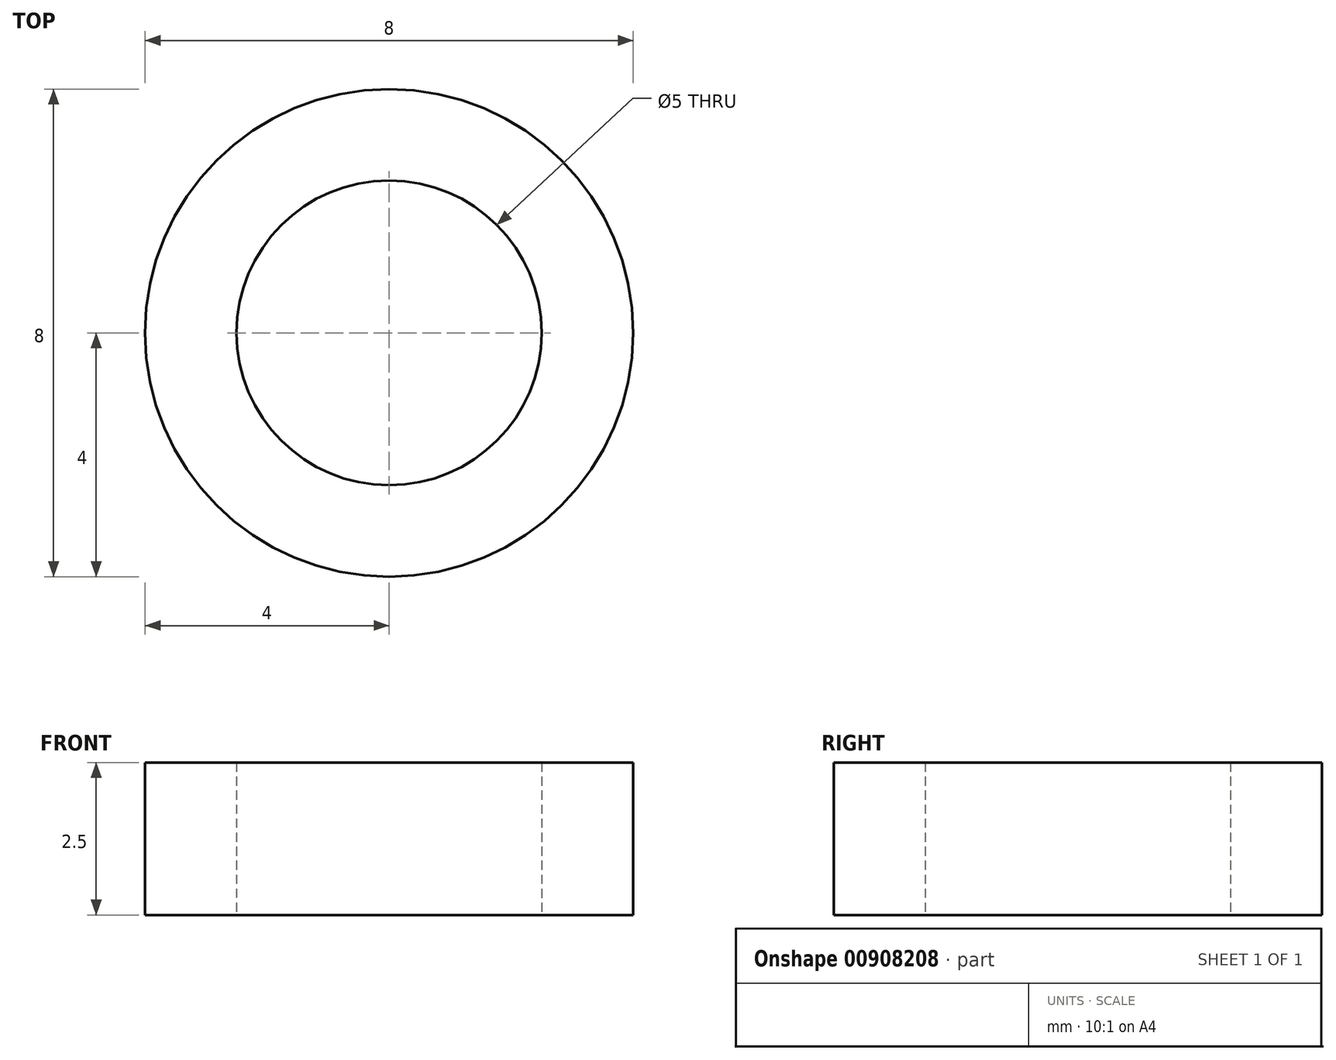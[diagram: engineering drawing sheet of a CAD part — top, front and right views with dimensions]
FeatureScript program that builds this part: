
annotation { "Feature Type Name" : "Feature", "Feature Type Description" : "" }
export const myFeature = defineFeature(function(context is Context, id is Id, definition is map)
    precondition{}
    {
        {
            var Q0;
            Q0=qCreatedBy(makeId("Top.planeOp"),FACE);
            var sketch = newSketch(context, id + "F0", { "sketchPlane" : qUnion([Q0])});
            skCircle(sketch, "E0", {"center": v(0, 0) * mm, "radius": 2.5 * mm});
            skCircle(sketch, "E1", {"center": v(0, 0) * mm, "radius": 4 * mm});
            skSolve(sketch);
        }
        {
            var Q0;
            Q0 = qSketchRegion(id + "F0", true);
            extrude(context, id + "F1", {"entities" : qUnion([Q0]), "depth" : 2.5 * mm, "offsetDistance" : 25 * mm, "symmetric" : true});
        }
    });
